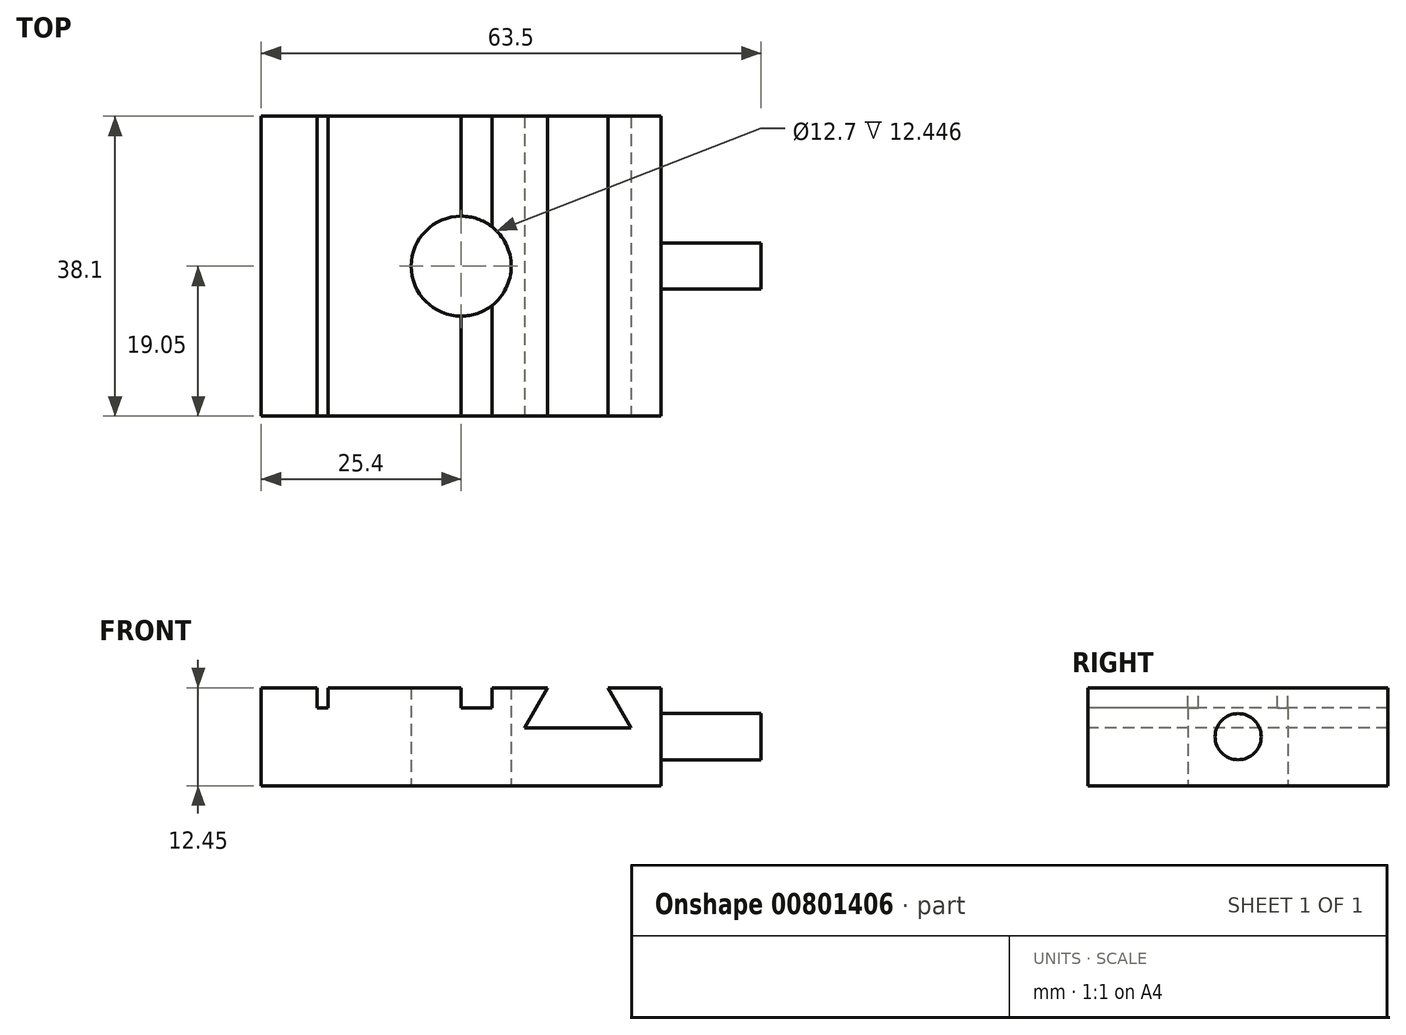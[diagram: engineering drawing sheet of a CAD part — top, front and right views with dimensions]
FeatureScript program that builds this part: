
annotation { "Feature Type Name" : "Feature", "Feature Type Description" : "" }
export const myFeature = defineFeature(function(context is Context, id is Id, definition is map)
    precondition{}
    {
        {
            var Q0;
            Q0=qCreatedBy(makeId("Top.planeOp"),FACE);
            var sketch = newSketch(context, id + "F0", { "sketchPlane" : qUnion([Q0])});
            skLineSegment(sketch, "E0.bottom", {"start": v(-25.4, 19.05) * mm, "end": v(25.4, 19.05) * mm});
            skLineSegment(sketch, "E0.top", {"start": v(-25.4, -19.05) * mm, "end": v(25.4, -19.05) * mm});
            skLineSegment(sketch, "E0.left", {"start": v(-25.4, 19.05) * mm, "end": v(-25.4, -19.05) * mm});
            skLineSegment(sketch, "E0.right", {"start": v(25.4, 19.05) * mm, "end": v(25.4, -19.05) * mm});
            skPoint(sketch, "E0.middle", {"position": v(0, 0) * mm});
            skCircle(sketch, "E1", {"center": v(0, 0) * mm, "radius": 6.35 * mm});
            skSolve(sketch);
        }
        {
            var Q0;
            Q0=makeQuery(id+"F0.imprint","IMPRINT",FACE,{"disambiguationData":[TD([[makeQuery(id+"F0.imprint","IMPRINT",EDGE,{"derivedFrom":sQuery(id+"F0.wireOp",EDGE,"E0.bottom")}),-1.0]])]});
            extrude(context, id + "F1", {"entities" : qUnion([Q0]), "depth" : 12.45 * mm, "offsetDistance" : 25.4 * mm});
        }
        {
            var Q0;
            Q0=makeQuery(id+"F1.opExtrude","CAP_FACE",FACE,{"disambiguationData":[OSD([sQuery(id+"F0.wireOp",EDGE,"E0.bottom"),sQuery(id+"F0.wireOp",EDGE,"E0.top"),sQuery(id+"F0.wireOp",EDGE,"E0.left"),sQuery(id+"F0.wireOp",EDGE,"E0.right"),sQuery(id+"F0.wireOp",EDGE,"E1")])],"isStart":false});
            var sketch = newSketch(context, id + "F2", { "sketchPlane" : qUnion([Q0])});
            skLineSegment(sketch, "E2.bottom", {"start": v(-18.32, 19.05) * mm, "end": v(-16.9, 19.05) * mm});
            skLineSegment(sketch, "E2.top", {"start": v(-18.32, -19.05) * mm, "end": v(-16.9, -19.05) * mm});
            skLineSegment(sketch, "E2.left", {"start": v(-18.32, 19.05) * mm, "end": v(-18.32, -19.05) * mm});
            skLineSegment(sketch, "E2.right", {"start": v(-16.9, 19.05) * mm, "end": v(-16.9, -19.05) * mm});
            skLineSegment(sketch, "E3.bottom", {"start": v(0, 19.05) * mm, "end": v(3.9, 19.05) * mm});
            skLineSegment(sketch, "E3.top", {"start": v(0, -19.05) * mm, "end": v(3.9, -19.05) * mm});
            skLineSegment(sketch, "E3.left", {"start": v(3.9, 19.05) * mm, "end": v(3.9, -19.05) * mm});
            skLineSegment(sketch, "E3.right", {"start": v(0, 19.05) * mm, "end": v(0, -19.05) * mm});
            skSolve(sketch);
        }
        {
            var Q0;
            Q0=makeQuery(id+"F2.imprint","IMPRINT",FACE,{"disambiguationData":[TD([[makeQuery(id+"F2.imprint","IMPRINT",EDGE,{"derivedFrom":sQuery(id+"F2.wireOp",EDGE,"E2.bottom")}),-1.0]])]});
            var Q1;
            {var subQ0=sQuery(id+"F2.wireOp",EDGE,"E3.bottom");Q1=makeQuery(id+"F2.imprint","IMPRINT",FACE,{"disambiguationData":[TD([[makeQuery(id+"F2.imprint","IMPRINT",EDGE,{"derivedFrom":subQ0}),-1.0]])]});}
            var Q2;
            {var subQ0=sQuery(id+"F2.wireOp",EDGE,"E3.top");Q2=makeQuery(id+"F2.imprint","IMPRINT",FACE,{"disambiguationData":[TD([[makeQuery(id+"F2.imprint","IMPRINT",EDGE,{"derivedFrom":subQ0}),1.0]])]});}
            extrude(context, id + "F3", {"entities" : qUnion([Q0, Q1, Q2]), "operationType" : NewBodyOperationType.REMOVE, "oppositeDirection" : true, "depth" : 2.54 * mm, "offsetDistance" : 25.4 * mm});
        }
        {
            var Q0;
            Q0=makeQuery(id+"F1.opExtrude","SWEPT_FACE",FACE,{"disambiguationData":[OSD([sQuery(id+"F0.wireOp",EDGE,"E0.top")])]});
            var sketch = newSketch(context, id + "F4", { "sketchPlane" : qUnion([Q0])});
            skLineSegment(sketch, "E4", {"start": v(11, 12.45) * mm, "end": v(8.07, 7.37) * mm});
            skLineSegment(sketch, "E5", {"start": v(8.07, 7.37) * mm, "end": v(21.55, 7.37) * mm});
            skLineSegment(sketch, "E6", {"start": v(21.55, 7.37) * mm, "end": v(18.62, 12.45) * mm});
            skLineSegment(sketch, "E7", {"start": v(14.8, 7.37) * mm, "end": v(14.8, 12.45) * mm});
            skSolve(sketch);
        }
        {
            var Q0;
            {var subQ0=sQuery(id+"F4.wireOp",EDGE,"E4");Q0=makeQuery(id+"F4.imprint","IMPRINT",FACE,{"disambiguationData":[TD([[makeQuery(id+"F4.imprint","IMPRINT",EDGE,{"derivedFrom":subQ0}),1.0]])]});}
            var Q1;
            {var subQ0=sQuery(id+"F4.wireOp",EDGE,"E6");Q1=makeQuery(id+"F4.imprint","IMPRINT",FACE,{"disambiguationData":[TD([[makeQuery(id+"F4.imprint","IMPRINT",EDGE,{"derivedFrom":subQ0}),1.0]])]});}
            extrude(context, id + "F5", {"entities" : qUnion([Q0, Q1]), "operationType" : NewBodyOperationType.REMOVE, "oppositeDirection" : true, "depth" : 38.1 * mm, "offsetDistance" : 25.4 * mm});
        }
        {
            var Q0;
            Q0=makeQuery(id+"F1.opExtrude","SWEPT_FACE",FACE,{"disambiguationData":[OSD([sQuery(id+"F0.wireOp",EDGE,"E0.right")])]});
            var sketch = newSketch(context, id + "F6", { "sketchPlane" : qUnion([Q0])});
            skCircle(sketch, "E8", {"center": v(0, 6.22) * mm, "radius": 2.93 * mm});
            skPoint(sketch, "E8.centerSnap0", {"position": v(-19.05, 6.22) * mm});
            skSolve(sketch);
        }
        {
            var Q0;
            Q0=makeQuery(id+"F6.imprint","IMPRINT",FACE,{"disambiguationData":[TD([[makeQuery(id+"F6.imprint","IMPRINT",EDGE,{"derivedFrom":sQuery(id+"F6.wireOp",EDGE,"E8")}),1.0]])]});
            extrude(context, id + "F7", {"entities" : qUnion([Q0]), "operationType" : NewBodyOperationType.ADD, "depth" : 12.7 * mm, "offsetDistance" : 25.4 * mm});
        }
    });
